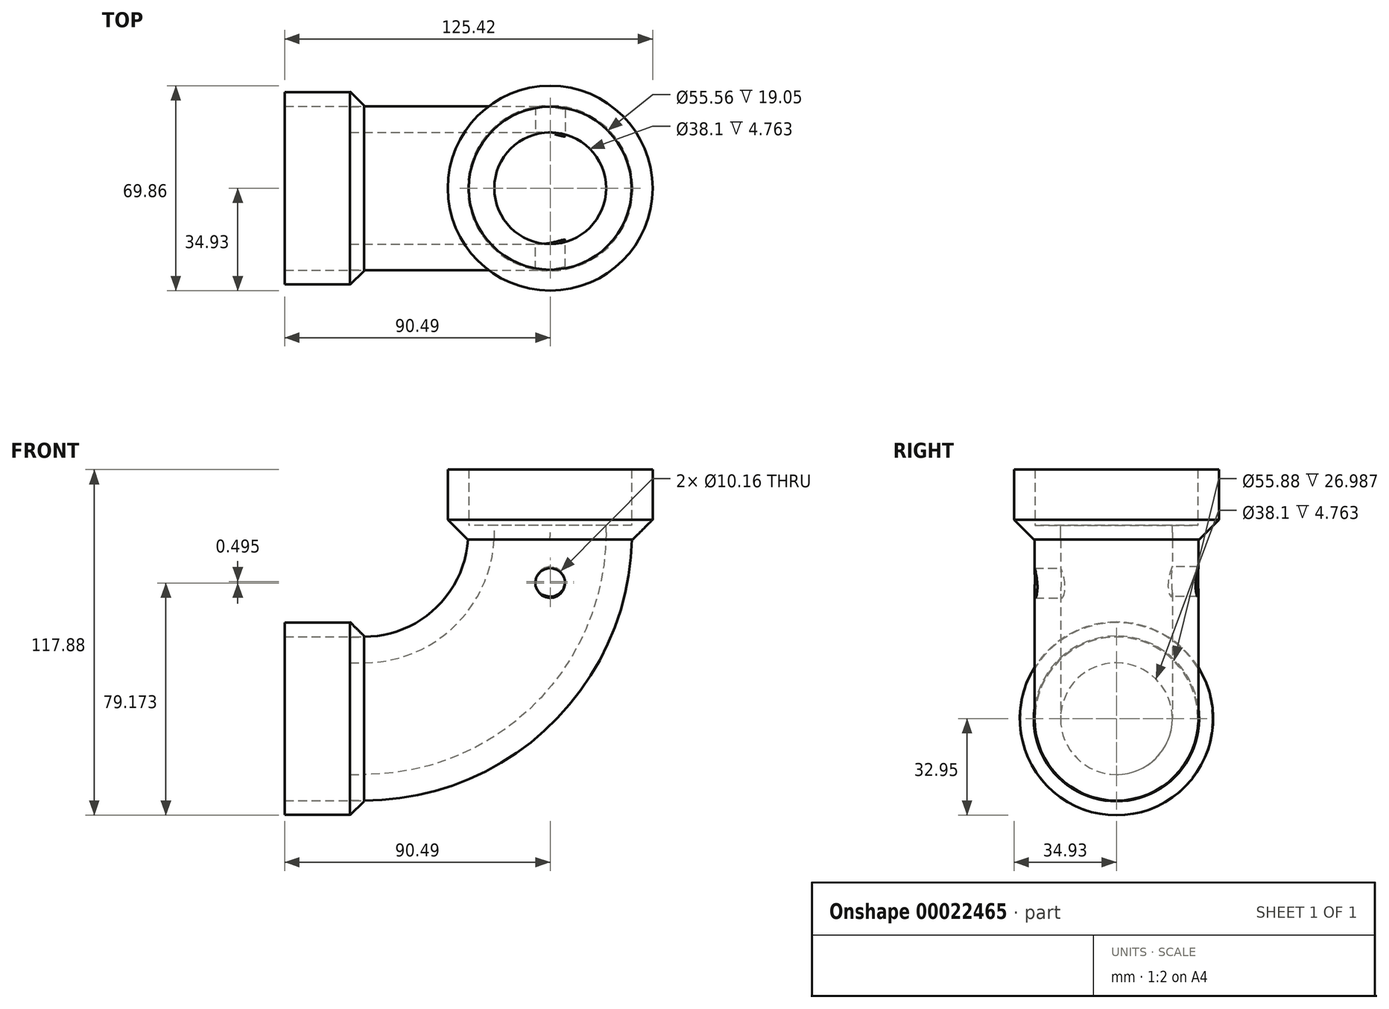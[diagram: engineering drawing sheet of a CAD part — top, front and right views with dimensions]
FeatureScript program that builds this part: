
annotation { "Feature Type Name" : "Feature", "Feature Type Description" : "" }
export const myFeature = defineFeature(function(context is Context, id is Id, definition is map)
    precondition{}
    {
        {
            var Q0;
            Q0=qCreatedBy(makeId("Top.planeOp"),FACE);
            var sketch = newSketch(context, id + "F0", { "sketchPlane" : qUnion([Q0])});
            skCircle(sketch, "E0", {"center": v(0, 0) * mm, "radius": 34.93 * mm});
            skCircle(sketch, "E1", {"center": v(0, 0) * mm, "radius": 27.78 * mm});
            skCircle(sketch, "E2", {"center": v(0, 0) * mm, "radius": 22.23 * mm});
            skSolve(sketch);
        }
        {
            var Q0;
            Q0=makeQuery(id+"F0.imprint","IMPRINT",FACE,{"disambiguationData":[TD([[makeQuery(id+"F0.imprint","IMPRINT",EDGE,{"derivedFrom":sQuery(id+"F0.wireOp",EDGE,"E0")}),1.0]])]});
            extrude(context, id + "F1", {"entities" : qUnion([Q0]), "depth" : 19.05 * mm});
        }
        {
            var Q0;
            Q0=qCreatedBy(makeId("Top.planeOp"),FACE);
            var sketch = newSketch(context, id + "F2", { "sketchPlane" : qUnion([Q0])});
            skCircle(sketch, "E3", {"center": v(0, 0) * mm, "radius": 22.23 * mm});
            skCircle(sketch, "E4", {"center": v(0, 0) * mm, "radius": 34.93 * mm});
            skSolve(sketch);
        }
        {
            var Q0;
            Q0=makeQuery(id+"F2.imprint","IMPRINT",FACE,{"disambiguationData":[TD([[makeQuery(id+"F2.imprint","IMPRINT",EDGE,{"derivedFrom":sQuery(id+"F2.wireOp",EDGE,"E3")}),-1.0]])]});
            extrude(context, id + "F3", {"entities" : qUnion([Q0]), "operationType" : NewBodyOperationType.ADD, "oppositeDirection" : true, "depth" : 4.76 * mm});
        }
        {
            var Q0;
            Q0=makeQuery(id+"F3.opExtrude","CAP_EDGE",EDGE,{"disambiguationData":[OSD([sQuery(id+"F2.wireOp",EDGE,"E4")])],"isStart":false});
            chamfer(context, id + "F4", {"entities" : qUnion([Q0]), "chamferType" : ChamferType.OFFSET_ANGLE, "width" : 6.74 * mm, "oppositeDirection" : false, "angle" : 45 * degree});
        }
        {
            var Q0;
            Q0=qCreatedBy(makeId("Top.planeOp"),FACE);
            var sketch = newSketch(context, id + "F5", { "sketchPlane" : qUnion([Q0])});
            skCircle(sketch, "E5", {"center": v(0, 0) * mm, "radius": 19.05 * mm});
            skCircle(sketch, "E6", {"center": v(0, 0) * mm, "radius": 28.2 * mm});
            skSolve(sketch);
        }
        {
            var Q0;
            Q0=makeQuery(id+"F5.imprint","IMPRINT",FACE,{"disambiguationData":[TD([[makeQuery(id+"F5.imprint","IMPRINT",EDGE,{"derivedFrom":sQuery(id+"F5.wireOp",EDGE,"E5")}),-1.0]])]});
            extrude(context, id + "F6", {"entities" : qUnion([Q0]), "operationType" : NewBodyOperationType.ADD, "oppositeDirection" : true, "depth" : 4.76 * mm});
        }
        {
            var Q0;
            Q0=qCreatedBy(makeId("Top.planeOp"),FACE);
            var sketch = newSketch(context, id + "F7", { "sketchPlane" : qUnion([Q0])});
            skCircle(sketch, "E7", {"center": v(0, 0) * mm, "radius": 19.05 * mm});
            skCircle(sketch, "E8", {"center": v(0, 0) * mm, "radius": 27.94 * mm});
            skSolve(sketch);
        }
        {
            var Q0;
            Q0=qCreatedBy(makeId("Front.planeOp"),FACE);
            var sketch = newSketch(context, id + "F8", { "sketchPlane" : qUnion([Q0])});
            skArc(sketch, "E9", {"start": v(-63.5, -65.88) * mm, "mid": v(-18.6, -47.28) * mm, "end": v(0, -2.38) * mm});
            skLineSegment(sketch, "E10", {"start": v(0, -2.38) * mm, "end": v(0, 0) * mm});
            skSolve(sketch);
        }
        {
            var Q0;
            Q0=qSketchRegion(id+"F7",true);
            var Q1;
            Q1=qConstructionFilter(qBodyType(qCreatedBy(id+"F8",EDGE),BodyType.WIRE),ConstructionObject.NO);
            sweep(context, id + "F9", {"operationType" : NewBodyOperationType.ADD, "profiles" : qUnion([Q0]), "path" : qUnion([Q1])});
        }
        {
            var Q0;
            Q0=makeQuery(id+"F9.opSweep","CAP_FACE",FACE,{"disambiguationData":[OSD([sQuery(id+"F7.wireOp",EDGE,"E7"),sQuery(id+"F7.wireOp",EDGE,"E8"),sQuery(id+"F8.wireOp",VERTEX,"E9.start")])],"isStart":false});
            var sketch = newSketch(context, id + "F10", { "sketchPlane" : qUnion([Q0])});
            skCircle(sketch, "E11", {"center": v(0, -65.88) * mm, "radius": 27.78 * mm});
            skCircle(sketch, "E12", {"center": v(0, -65.88) * mm, "radius": 34.93 * mm});
            skCircle(sketch, "E13", {"center": v(0, -65.88) * mm, "radius": 19.05 * mm});
            skSolve(sketch);
        }
        {
            var Q0;
            Q0=makeQuery(id+"F10.imprint","IMPRINT",FACE,{"disambiguationData":[TD([[makeQuery(id+"F10.imprint","IMPRINT",EDGE,{"derivedFrom":sQuery(id+"F10.wireOp",EDGE,"E12")}),1.0]])]});
            var Q1;
            Q1=makeQuery(id+"F10.imprint","IMPRINT",FACE,{"disambiguationData":[TD([[makeQuery(id+"F10.imprint","IMPRINT",EDGE,{"derivedFrom":sQuery(id+"F10.wireOp",EDGE,"E11")}),1.0]])]});
            extrude(context, id + "F11", {"entities" : qUnion([Q0, Q1]), "operationType" : NewBodyOperationType.ADD, "depth" : 4.76 * mm});
        }
        {
            var Q0;
            Q0=makeQuery(id+"F11.opExtrude","CAP_EDGE",EDGE,{"disambiguationData":[OSD([sQuery(id+"F10.wireOp",EDGE,"E12")])],"isStart":true});
            chamfer(context, id + "F12", {"entities" : qUnion([Q0]), "width" : 6.74 * mm, "tangentPropagation" : true});
        }
        {
            var Q0;
            Q0=makeQuery(id+"F11.opExtrude","CAP_FACE",FACE,{"disambiguationData":[OSD([sQuery(id+"F7.wireOp",EDGE,"E8"),sQuery(id+"F8.wireOp",VERTEX,"E9.start"),sQuery(id+"F10.wireOp",EDGE,"E12")])],"isStart":false});
            var sketch = newSketch(context, id + "F13", { "sketchPlane" : qUnion([Q0])});
            skCircle(sketch, "E14", {"center": v(0, -65.88) * mm, "radius": 27.78 * mm});
            skCircle(sketch, "E15", {"center": v(0, -65.88) * mm, "radius": 32.73 * mm});
            skSolve(sketch);
        }
        {
            var Q0;
            Q0=makeQuery(id+"F13.imprint","IMPRINT",FACE,{"disambiguationData":[TD([[makeQuery(id+"F13.imprint","IMPRINT",EDGE,{"derivedFrom":sQuery(id+"F13.wireOp",EDGE,"E15")}),1.0]])]});
            extrude(context, id + "F14", {"entities" : qUnion([Q0]), "operationType" : NewBodyOperationType.ADD, "depth" : 22.22 * mm});
        }
        {
            var Q0;
            Q0=qCreatedBy(makeId("Front.planeOp"),FACE);
            var sketch = newSketch(context, id + "F15", { "sketchPlane" : qUnion([Q0])});
            skPoint(sketch, "E16", {"position": v(0, -19.66) * mm});
            skSolve(sketch);
        }
        {
            var Q0;
            Q0=sQuery(id+"F15.wireOp",VERTEX,"E16");
            var Q1;
            Q1=makeQuery(id+"F1.opExtrude","SWEPT_BODY",BODY,{"disambiguationData":[OSD([sQuery(id+"F0.wireOp",EDGE,"E0"),sQuery(id+"F0.wireOp",EDGE,"E1")])]});
            hole(context, id + "F16", {"style" : HoleStyle.SIMPLE, "holeDiameter" : 10.16 * mm, "endStyle" : HoleEndStyle.THROUGH, "oppositeDirection" : true, "locations" : qUnion([Q0]), "scope" : qUnion([Q1])});
        }
        {
            var Q0;
            Q0=qCreatedBy(makeId("Front.planeOp"),FACE);
            var sketch = newSketch(context, id + "F17", { "sketchPlane" : qUnion([Q0])});
            skPoint(sketch, "E17", {"position": v(0, -19.16) * mm});
            skSolve(sketch);
        }
        {
            var Q0;
            Q0=sQuery(id+"F17.wireOp",VERTEX,"E17");
            var Q1;
            Q1=makeQuery(id+"F1.opExtrude","SWEPT_BODY",BODY,{"disambiguationData":[OSD([sQuery(id+"F0.wireOp",EDGE,"E0"),sQuery(id+"F0.wireOp",EDGE,"E1")])]});
            hole(context, id + "F18", {"style" : HoleStyle.SIMPLE, "holeDiameter" : 10.16 * mm, "endStyle" : HoleEndStyle.THROUGH, "locations" : qUnion([Q0]), "scope" : qUnion([Q1])});
        }
    });
